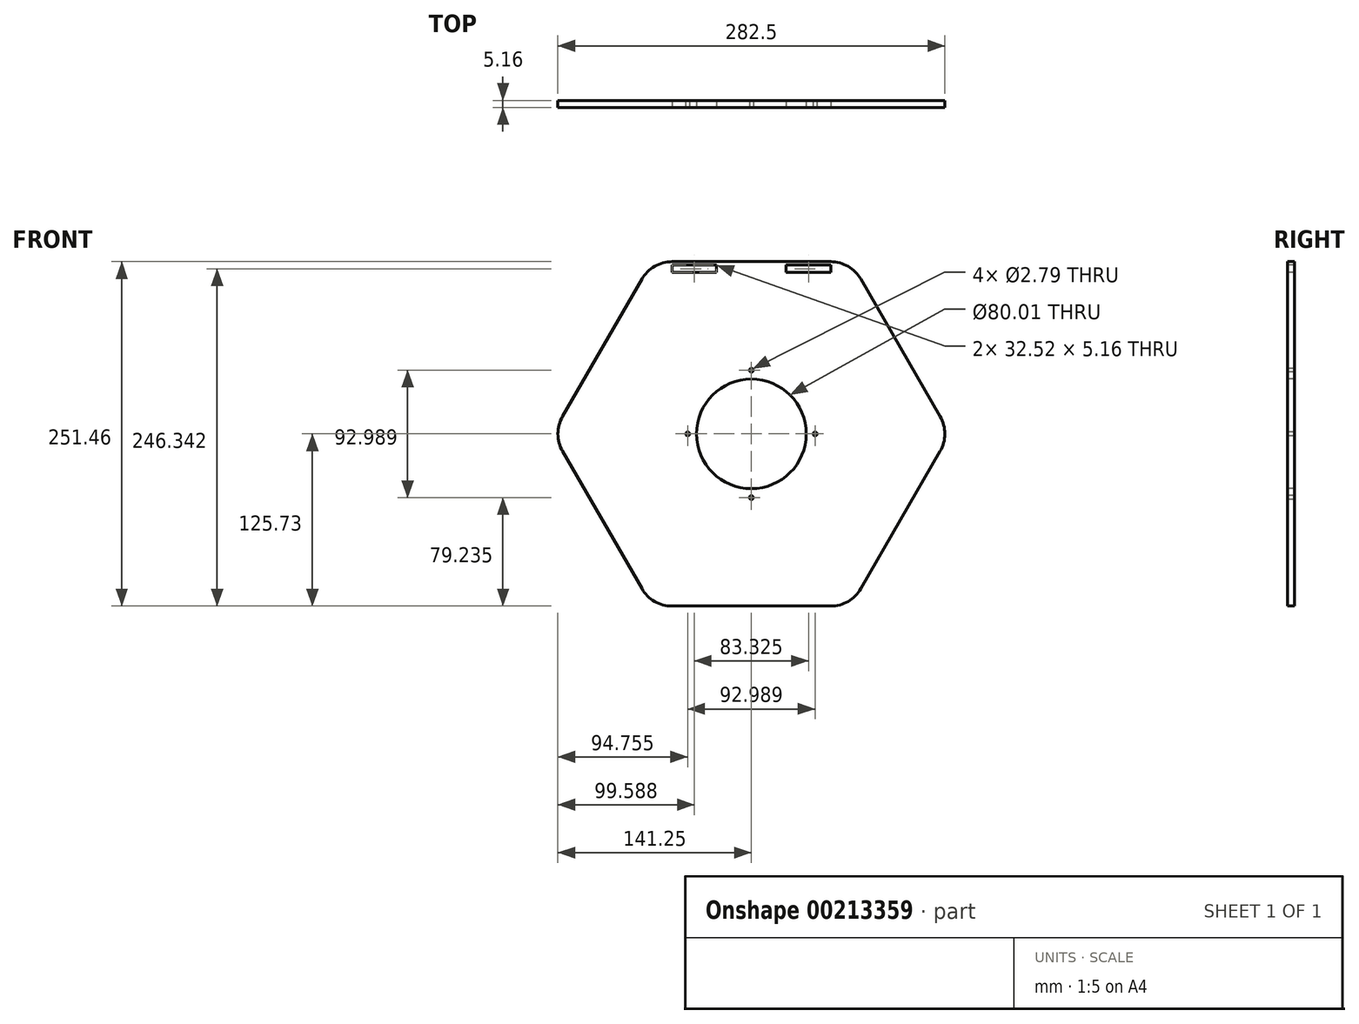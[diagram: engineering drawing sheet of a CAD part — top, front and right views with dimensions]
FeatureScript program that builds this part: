
annotation { "Feature Type Name" : "Feature", "Feature Type Description" : "" }
export const myFeature = defineFeature(function(context is Context, id is Id, definition is map)
    precondition{}
    {
        {
            var Q0;
            Q0=qCreatedBy(makeId("Front.planeOp"),FACE);
            var sketch = newSketch(context, id + "F0", { "sketchPlane" : qUnion([Q0])});
            skCircle(sketch, "E0.cCircle", {"center": v(0, 0) * mm, "radius": 125.73 * mm, "construction": true});
            skLineSegment(sketch, "E0.0", {"start": v(79.92, 113.03) * mm, "end": v(137.85, 12.7) * mm});
            skLineSegment(sketch, "E0.1", {"start": v(137.85, -12.7) * mm, "end": v(79.92, -113.03) * mm});
            skLineSegment(sketch, "E0.2", {"start": v(57.93, -125.73) * mm, "end": v(-57.93, -125.73) * mm});
            skLineSegment(sketch, "E0.3", {"start": v(-79.92, -113.03) * mm, "end": v(-137.85, -12.7) * mm});
            skLineSegment(sketch, "E0.4", {"start": v(-137.85, 12.7) * mm, "end": v(-79.92, 113.03) * mm});
            skLineSegment(sketch, "E0.5", {"start": v(-57.93, 125.73) * mm, "end": v(57.93, 125.73) * mm});
            skPoint(sketch, "E0.0.midPoint", {"position": v(108.89, 62.87) * mm});
            skPoint(sketch, "E1.visualSharp", {"position": v(-72.6, 125.73) * mm});
            skArc(sketch, "E1.filletArc", {"start": v(-57.93, 125.73) * mm, "mid": v(-70.63, 122.33) * mm, "end": v(-79.92, 113.03) * mm});
            skPoint(sketch, "E2.visualSharp", {"position": v(72.6, 125.73) * mm});
            skArc(sketch, "E2.filletArc", {"start": v(79.92, 113.03) * mm, "mid": v(70.63, 122.33) * mm, "end": v(57.93, 125.73) * mm});
            skPoint(sketch, "E3.visualSharp", {"position": v(145.18, 0) * mm});
            skArc(sketch, "E3.filletArc", {"start": v(137.85, -12.7) * mm, "mid": v(141.25, 0) * mm, "end": v(137.85, 12.7) * mm});
            skPoint(sketch, "E4.visualSharp", {"position": v(72.6, -125.73) * mm});
            skArc(sketch, "E4.filletArc", {"start": v(57.93, -125.73) * mm, "mid": v(70.63, -122.33) * mm, "end": v(79.92, -113.03) * mm});
            skPoint(sketch, "E5.visualSharp", {"position": v(-72.6, -125.73) * mm});
            skArc(sketch, "E5.filletArc", {"start": v(-79.92, -113.03) * mm, "mid": v(-70.63, -122.33) * mm, "end": v(-57.93, -125.73) * mm});
            skPoint(sketch, "E6.visualSharp", {"position": v(-145.18, 0) * mm});
            skArc(sketch, "E6.filletArc", {"start": v(-137.85, 12.7) * mm, "mid": v(-141.25, 0) * mm, "end": v(-137.85, -12.7) * mm});
            skSolve(sketch);
        }
        {
            var Q0;
            Q0=makeQuery(id+"F0.imprint","IMPRINT",FACE,{"disambiguationData":[TD([[makeQuery(id+"F0.imprint","IMPRINT",EDGE,{"derivedFrom":sQuery(id+"F0.wireOp",EDGE,"E0.0")}),-1.0]])]});
            extrude(context, id + "F1", {"entities" : qUnion([Q0]), "oppositeDirection" : true, "depth" : 5.16 * mm});
        }
        {
            var Q0;
            Q0=makeQuery(id+"F1.opExtrude","CAP_FACE",FACE,{"disambiguationData":[OSD([sQuery(id+"F0.wireOp",EDGE,"E0.0"),sQuery(id+"F0.wireOp",EDGE,"E0.1"),sQuery(id+"F0.wireOp",EDGE,"E0.2"),sQuery(id+"F0.wireOp",EDGE,"E0.3"),sQuery(id+"F0.wireOp",EDGE,"E0.4"),sQuery(id+"F0.wireOp",EDGE,"E0.5"),sQuery(id+"F0.wireOp",EDGE,"E1.filletArc"),sQuery(id+"F0.wireOp",EDGE,"E2.filletArc"),sQuery(id+"F0.wireOp",EDGE,"E3.filletArc"),sQuery(id+"F0.wireOp",EDGE,"E4.filletArc"),sQuery(id+"F0.wireOp",EDGE,"E5.filletArc"),sQuery(id+"F0.wireOp",EDGE,"E6.filletArc")])],"isStart":true});
            var sketch = newSketch(context, id + "F2", { "sketchPlane" : qUnion([Q0])});
            skCircle(sketch, "E7", {"center": v(0, 0) * mm, "radius": 40 * mm});
            skCircle(sketch, "E8", {"center": v(0, 0) * mm, "radius": 46.5 * mm, "construction": true});
            skCircle(sketch, "E9", {"center": v(0, 0) * mm, "radius": 51.75 * mm, "construction": true});
            skCircle(sketch, "E10", {"center": v(0, 46.5) * mm, "radius": 1.4 * mm});
            skCircle(sketch, "E11.1.0", {"center": v(-46.5, 0) * mm, "radius": 1.4 * mm});
            skCircle(sketch, "E11.2.0", {"center": v(0, -46.5) * mm, "radius": 1.4 * mm});
            skCircle(sketch, "E11.3.0", {"center": v(46.5, 0) * mm, "radius": 1.4 * mm});
            skSolve(sketch);
        }
        {
            var Q0;
            Q0 = qSketchRegion(id + "F2", true);
            extrude(context, id + "F3", {"entities" : qUnion([Q0]), "operationType" : NewBodyOperationType.REMOVE, "endBound" : BoundingType.THROUGH_ALL, "oppositeDirection" : true, "depth" : 25.4 * mm});
        }
        {
            var Q0;
            Q0=makeQuery(id+"F1.opExtrude","CAP_FACE",FACE,{"disambiguationData":[OSD([sQuery(id+"F0.wireOp",EDGE,"E0.0"),sQuery(id+"F0.wireOp",EDGE,"E0.1"),sQuery(id+"F0.wireOp",EDGE,"E0.2"),sQuery(id+"F0.wireOp",EDGE,"E0.3"),sQuery(id+"F0.wireOp",EDGE,"E0.4"),sQuery(id+"F0.wireOp",EDGE,"E0.5"),sQuery(id+"F0.wireOp",EDGE,"E1.filletArc"),sQuery(id+"F0.wireOp",EDGE,"E2.filletArc"),sQuery(id+"F0.wireOp",EDGE,"E3.filletArc"),sQuery(id+"F0.wireOp",EDGE,"E4.filletArc"),sQuery(id+"F0.wireOp",EDGE,"E5.filletArc"),sQuery(id+"F0.wireOp",EDGE,"E6.filletArc")])],"isStart":true});
            var sketch = newSketch(context, id + "F4", { "sketchPlane" : qUnion([Q0])});
            skLineSegment(sketch, "E12.bottom", {"start": v(-57.92, 123.19) * mm, "end": v(57.92, 123.19) * mm});
            skLineSegment(sketch, "E12.top", {"start": v(-57.92, 118.03) * mm, "end": v(57.92, 118.03) * mm});
            skLineSegment(sketch, "E12.left", {"start": v(-57.92, 123.19) * mm, "end": v(-57.92, 118.03) * mm});
            skLineSegment(sketch, "E12.right", {"start": v(57.92, 123.19) * mm, "end": v(57.92, 118.03) * mm});
            skPoint(sketch, "E13", {"position": v(0, 123.19) * mm});
            skPoint(sketch, "E14", {"position": v(0, 125.73) * mm});
            skLineSegment(sketch, "E15.bottom", {"start": v(-25.4, 123.19) * mm, "end": v(25.4, 123.19) * mm});
            skLineSegment(sketch, "E15.top", {"start": v(-25.4, 118.03) * mm, "end": v(25.4, 118.03) * mm});
            skLineSegment(sketch, "E15.left", {"start": v(-25.4, 123.19) * mm, "end": v(-25.4, 118.03) * mm});
            skLineSegment(sketch, "E15.right", {"start": v(25.4, 123.19) * mm, "end": v(25.4, 118.03) * mm});
            skSolve(sketch);
        }
        {
            var Q0;
            {var subQ0=sQuery(id+"F4.wireOp",EDGE,"E12.left");Q0=makeQuery(id+"F4.imprint","IMPRINT",FACE,{"disambiguationData":[TD([[makeQuery(id+"F4.imprint","IMPRINT",EDGE,{"derivedFrom":subQ0}),1.0]])]});}
            var Q1;
            {var subQ0=sQuery(id+"F4.wireOp",EDGE,"E12.right");Q1=makeQuery(id+"F4.imprint","IMPRINT",FACE,{"disambiguationData":[TD([[makeQuery(id+"F4.imprint","IMPRINT",EDGE,{"derivedFrom":subQ0}),-1.0]])]});}
            extrude(context, id + "F5", {"entities" : qUnion([Q0, Q1]), "operationType" : NewBodyOperationType.REMOVE, "endBound" : BoundingType.THROUGH_ALL, "oppositeDirection" : true, "depth" : 25.4 * mm});
        }
        {
            var Q0;
            Q0=qCreatedBy(makeId("Right.planeOp"),FACE);
            var sketch = newSketch(context, id + "F6", { "sketchPlane" : qUnion([Q0])});
            skLineSegment(sketch, "E16", {"start": v(0, 0) * mm, "end": v(-137.26, 0) * mm, "construction": true});
            skSolve(sketch);
        }
    });
